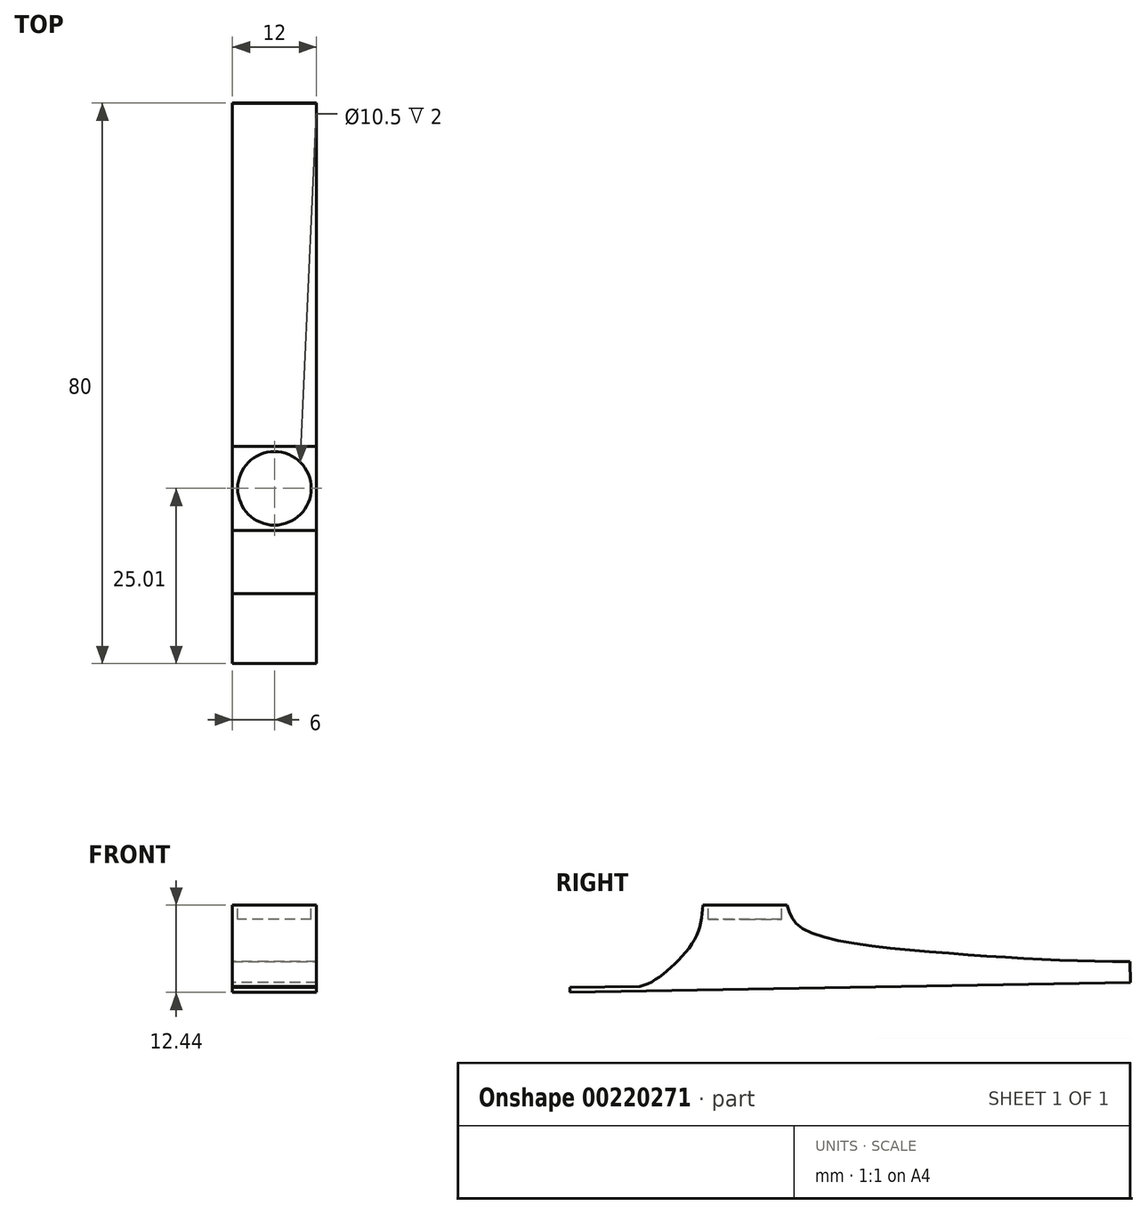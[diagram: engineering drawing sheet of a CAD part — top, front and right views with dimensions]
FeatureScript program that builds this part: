
annotation { "Feature Type Name" : "Feature", "Feature Type Description" : "" }
export const myFeature = defineFeature(function(context is Context, id is Id, definition is map)
    precondition{}
    {
        {
            var Q0;
            Q0=qCreatedBy(makeId("Right.planeOp"),FACE);
            var sketch = newSketch(context, id + "F0", { "sketchPlane" : qUnion([Q0])});
            skLineSegment(sketch, "E0", {"start": v(-6, 0) * mm, "end": v(6, 0) * mm});
            skLineSegment(sketch, "E1", {"start": v(-25, -12.44) * mm, "end": v(54.99, -11.04) * mm});
            skLineSegment(sketch, "E2", {"start": v(-25, -12.44) * mm, "end": v(-25.01, -11.74) * mm});
            skLineSegment(sketch, "E3", {"start": v(-25.01, -11.74) * mm, "end": v(-15.01, -11.56) * mm});
            skPoint(sketch, "E4", {"position": v(0, -12) * mm});
            skFitSpline(sketch, "E5", {"points": [v(-15.01, -11.56) * mm, v(-10.91, -9.17) * mm, v(-6.96, -4.41) * mm, v(-6, 0) * mm], "startDerivative": vector(13.31, 2.48) * mm, "endDerivative": vector(1.31, 13.6) * mm});
            skFitSpline(sketch, "E6", {"points": [v(6, 0) * mm, v(8.1, -3.25) * mm, v(28.89, -6.83) * mm, v(54.97, -8.04) * mm], "startDerivative": vector(6.15, -20.62) * mm, "endDerivative": vector(57.49, 0.33) * mm});
            skLineSegment(sketch, "E7", {"start": v(54.99, -11.04) * mm, "end": v(54.97, -8.04) * mm});
            skSolve(sketch);
        }
        {
            var Q0;
            Q0=qSketchRegion(id+"F0",true);
            extrude(context, id + "F1", {"entities" : qUnion([Q0]), "depth" : 12 * mm});
        }
        {
            var Q0;
            Q0=makeQuery(id+"F1.opExtrude","SWEPT_FACE",FACE,{"disambiguationData":[OSD([sQuery(id+"F0.wireOp",EDGE,"E0")])]});
            var sketch = newSketch(context, id + "F2", { "sketchPlane" : qUnion([Q0])});
            skCircle(sketch, "E8", {"center": v(6, 0) * mm, "radius": 5.25 * mm});
            skPoint(sketch, "E8.centerSnap0", {"position": v(6, -6) * mm});
            skPoint(sketch, "E8.centerSnap1", {"position": v(12, 0) * mm});
            skSolve(sketch);
        }
        {
            var Q0;
            Q0=makeQuery(id+"F2.imprint","IMPRINT",FACE,{"disambiguationData":[TD([[makeQuery(id+"F2.imprint","IMPRINT",EDGE,{"derivedFrom":sQuery(id+"F2.wireOp",EDGE,"E8")}),1.0]])]});
            extrude(context, id + "F3", {"entities" : qUnion([Q0]), "operationType" : NewBodyOperationType.REMOVE, "oppositeDirection" : true, "depth" : 2 * mm});
        }
    });
